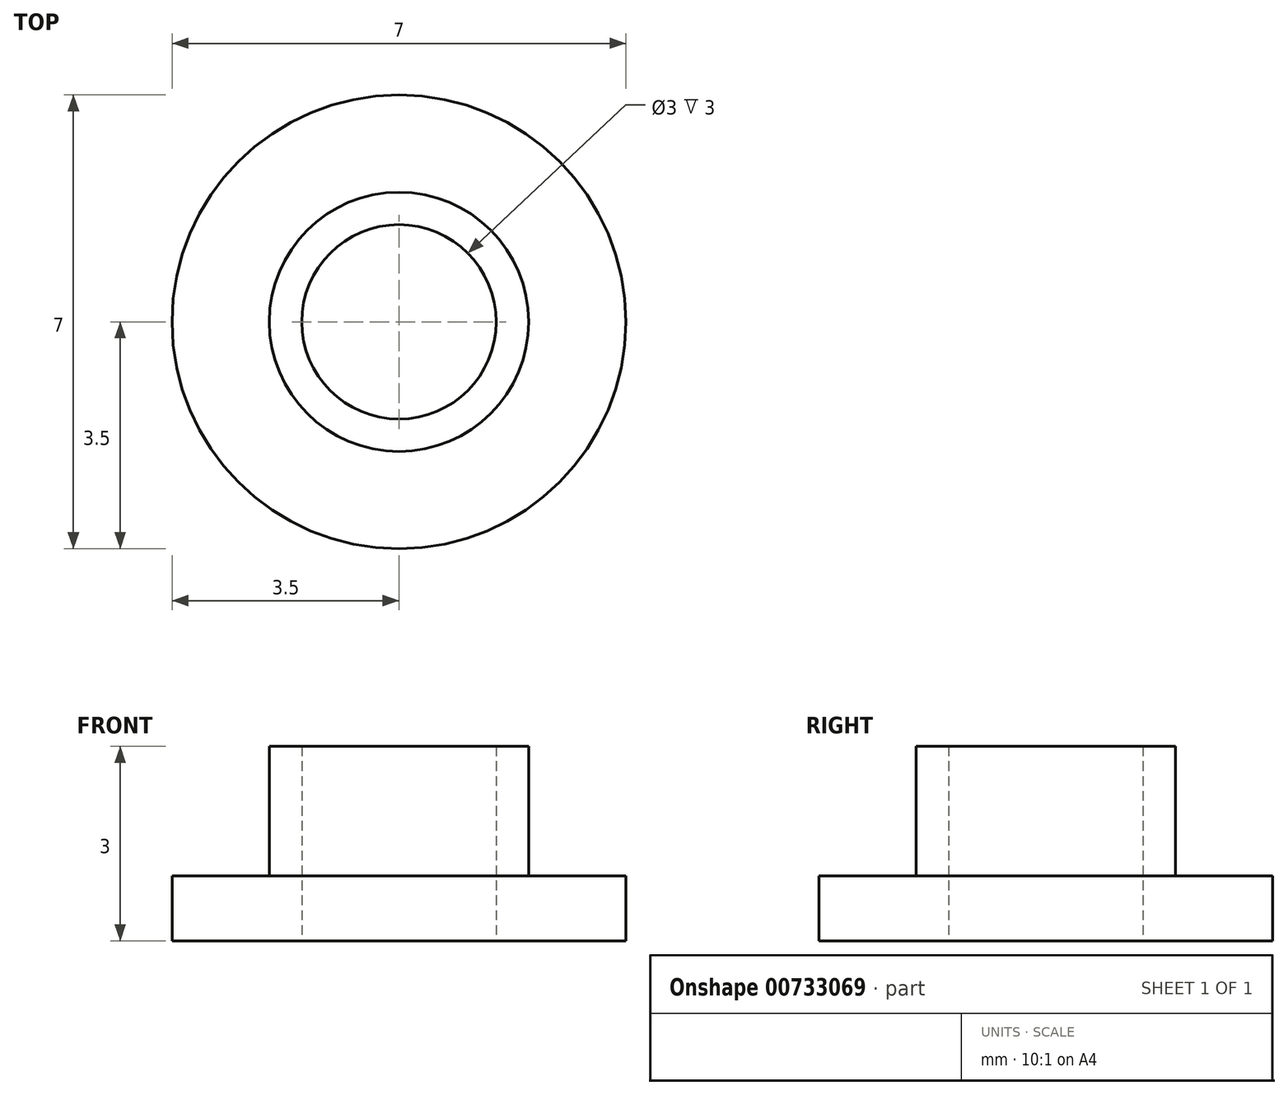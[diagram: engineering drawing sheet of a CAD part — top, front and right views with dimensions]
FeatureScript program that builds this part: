
annotation { "Feature Type Name" : "Feature", "Feature Type Description" : "" }
export const myFeature = defineFeature(function(context is Context, id is Id, definition is map)
    precondition{}
    {
        {
            var Q0;
            Q0=qCreatedBy(makeId("Top.planeOp"),FACE);
            var sketch = newSketch(context, id + "F0", { "sketchPlane" : qUnion([Q0])});
            skCircle(sketch, "E0", {"center": v(0, 0) * mm, "radius": 3.5 * mm});
            skCircle(sketch, "E1", {"center": v(0, 0) * mm, "radius": 2 * mm});
            skCircle(sketch, "E2", {"center": v(0, 0) * mm, "radius": 1.5 * mm});
            skSolve(sketch);
        }
        {
            var Q0;
            Q0=qSketchRegion(id+"F0",true);
            extrude(context, id + "F1", {"entities" : qUnion([Q0]), "depth" : 1 * mm, "offsetDistance" : 25 * mm});
        }
        {
            var Q0;
            Q0=makeQuery(id+"F0.imprint","IMPRINT",FACE,{"disambiguationData":[TD([[makeQuery(id+"F0.imprint","IMPRINT",EDGE,{"derivedFrom":sQuery(id+"F0.wireOp",EDGE,"E1")}),1.0]])]});
            extrude(context, id + "F2", {"entities" : qUnion([Q0]), "operationType" : NewBodyOperationType.ADD, "depth" : 3 * mm, "offsetDistance" : 25 * mm});
        }
    });
